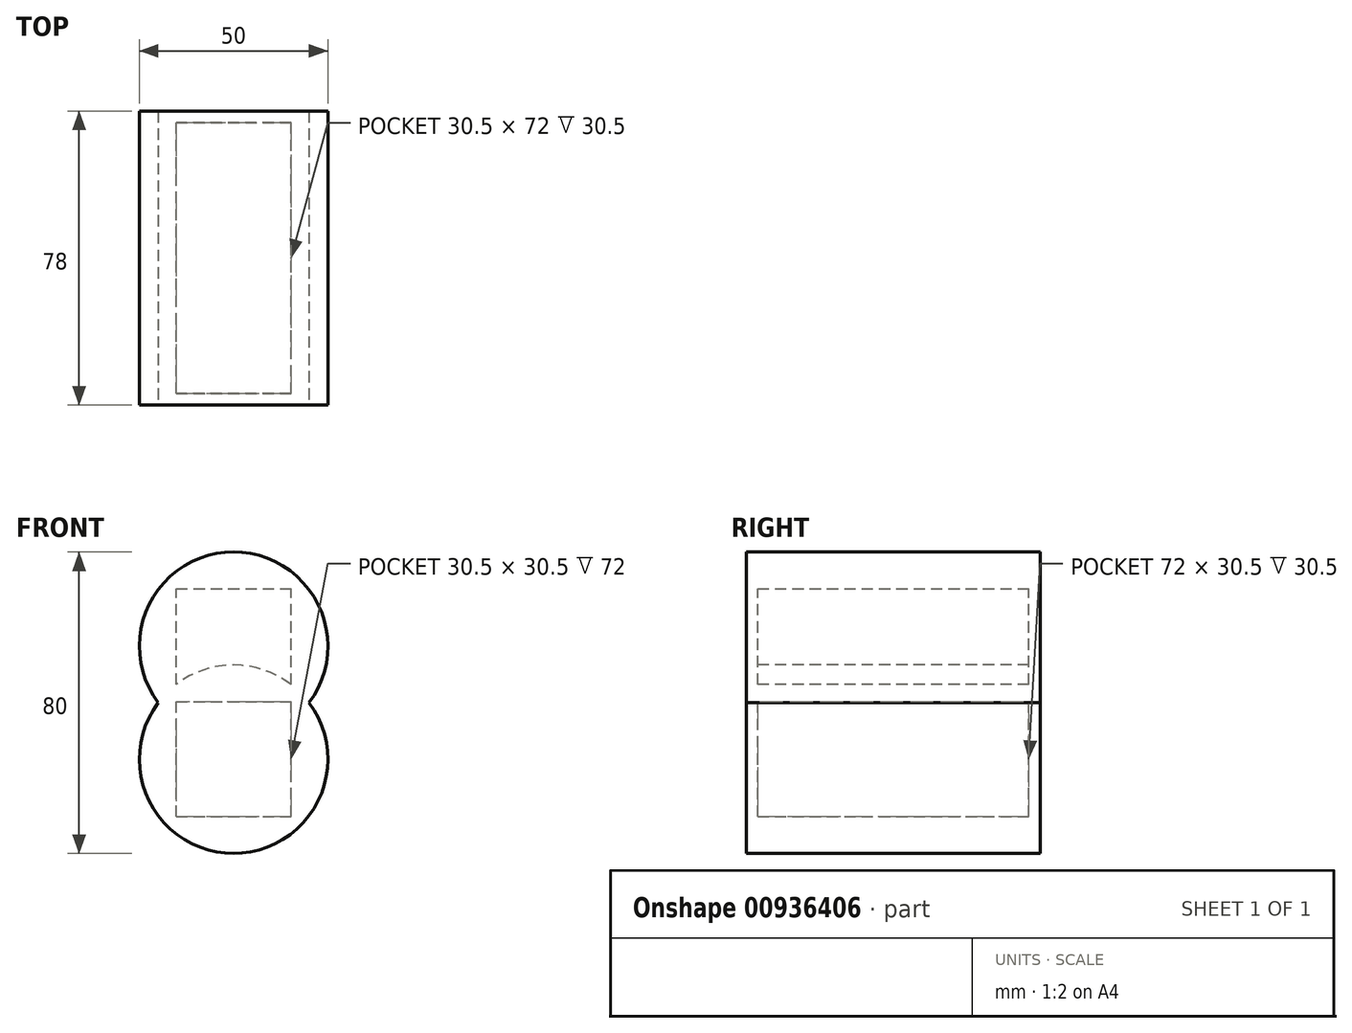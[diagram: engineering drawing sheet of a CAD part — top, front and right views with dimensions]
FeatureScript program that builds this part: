
annotation { "Feature Type Name" : "Feature", "Feature Type Description" : "" }
export const myFeature = defineFeature(function(context is Context, id is Id, definition is map)
    precondition{}
    {
        {
            var Q0;
            Q0=qCreatedBy(makeId("Front.planeOp"),FACE);
            var sketch = newSketch(context, id + "F0", { "sketchPlane" : qUnion([Q0])});
            skCircle(sketch, "E0", {"center": v(0, 0) * mm, "radius": 25 * mm});
            skSolve(sketch);
        }
        {
            var Q0;
            Q0 = qSketchRegion(id + "F0", true);
            extrude(context, id + "F1", {"entities" : qUnion([Q0]), "oppositeDirection" : true, "depth" : 75 * mm, "offsetDistance" : 25.4 * mm});
        }
        {
            var Q0;
            Q0=makeQuery(id+"F1.opExtrude","CAP_FACE",FACE,{"disambiguationData":[OSD([sQuery(id+"F0.wireOp",EDGE,"E0")])],"isStart":false});
            var sketch = newSketch(context, id + "F2", { "sketchPlane" : qUnion([Q0])});
            skLineSegment(sketch, "E1.bottom", {"start": v(15.25, -15.25) * mm, "end": v(-15.25, -15.25) * mm});
            skLineSegment(sketch, "E1.top", {"start": v(15.25, 15.25) * mm, "end": v(-15.25, 15.25) * mm});
            skLineSegment(sketch, "E1.left", {"start": v(15.25, -15.25) * mm, "end": v(15.25, 15.25) * mm});
            skLineSegment(sketch, "E1.right", {"start": v(-15.25, -15.25) * mm, "end": v(-15.25, 15.25) * mm});
            skPoint(sketch, "E1.middle", {"position": v(0, 0) * mm});
            skSolve(sketch);
        }
        {
            var Q0;
            Q0 = qSketchRegion(id + "F2", true);
            var Q1;
            Q1=makeQuery(id+"F1.opExtrude","CAP_FACE",FACE,{"disambiguationData":[OSD([sQuery(id+"F0.wireOp",EDGE,"E0")])],"isStart":true});
            extrude(context, id + "F3", {"entities" : qUnion([Q0]), "operationType" : NewBodyOperationType.REMOVE, "endBound" : BoundingType.UP_TO_SURFACE, "oppositeDirection" : true, "depth" : 194 * mm, "endBoundEntityFace" : qUnion([Q1]), "hasOffset" : true, "offsetDistance" : 3 * mm});
        }
        {
            var Q0;
            Q0=makeQuery(id+"F1.opExtrude","CAP_FACE",FACE,{"disambiguationData":[OSD([sQuery(id+"F0.wireOp",EDGE,"E0")])],"isStart":false});
            var sketch = newSketch(context, id + "F4", { "sketchPlane" : qUnion([Q0])});
            skCircle(sketch, "E2", {"center": v(0, 0) * mm, "radius": 25 * mm});
            skSolve(sketch);
        }
        {
            var Q0;
            Q0 = qSketchRegion(id + "F4", true);
            extrude(context, id + "F5", {"entities" : qUnion([Q0]), "operationType" : NewBodyOperationType.ADD, "depth" : 3 * mm, "offsetDistance" : 25 * mm});
        }
        {
            var Q0;
            Q0=qCreatedBy(makeId("Front.planeOp"),FACE);
            var sketch = newSketch(context, id + "F6", { "sketchPlane" : qUnion([Q0])});
            skCircle(sketch, "E3", {"center": v(0, -30) * mm, "radius": 25 * mm});
            skSolve(sketch);
        }
        {
            var Q0;
            Q0 = qSketchRegion(id + "F6", true);
            extrude(context, id + "F7", {"entities" : qUnion([Q0]), "operationType" : NewBodyOperationType.ADD, "oppositeDirection" : true, "depth" : 75 * mm, "offsetDistance" : 25 * mm});
        }
        {
            var Q0;
            Q0=makeQuery(id+"F7.opExtrude","CAP_FACE",FACE,{"disambiguationData":[OSD([sQuery(id+"F6.wireOp",EDGE,"E3")])],"isStart":false});
            var sketch = newSketch(context, id + "F8", { "sketchPlane" : qUnion([Q0])});
            skLineSegment(sketch, "E4.bottom", {"start": v(15.25, -45.25) * mm, "end": v(-15.25, -45.25) * mm});
            skLineSegment(sketch, "E4.top", {"start": v(15.25, -14.75) * mm, "end": v(-15.25, -14.75) * mm});
            skLineSegment(sketch, "E4.left", {"start": v(15.25, -45.25) * mm, "end": v(15.25, -14.75) * mm});
            skLineSegment(sketch, "E4.right", {"start": v(-15.25, -45.25) * mm, "end": v(-15.25, -14.75) * mm});
            skPoint(sketch, "E4.middle", {"position": v(0, -30) * mm});
            skSolve(sketch);
        }
        {
            var Q0;
            Q0 = qSketchRegion(id + "F8", true);
            var Q1;
            Q1=makeQuery(id+"F7.boolean.opBoolean","MERGE",FACE,{"derivedFrom":[makeQuery(id+"F1.opExtrude","CAP_FACE",FACE,{"disambiguationData":[OSD([sQuery(id+"F0.wireOp",EDGE,"E0")])],"isStart":true}),makeQuery(id+"F7.opExtrude","CAP_FACE",FACE,{"disambiguationData":[OSD([sQuery(id+"F6.wireOp",EDGE,"E3")])],"isStart":true})]});
            extrude(context, id + "F9", {"entities" : qUnion([Q0]), "operationType" : NewBodyOperationType.REMOVE, "endBound" : BoundingType.UP_TO_SURFACE, "oppositeDirection" : true, "depth" : 25 * mm, "endBoundEntityFace" : qUnion([Q1]), "hasOffset" : true, "offsetDistance" : 3 * mm});
        }
        {
            var Q0;
            Q0=makeQuery(id+"F7.opExtrude","CAP_FACE",FACE,{"disambiguationData":[OSD([sQuery(id+"F6.wireOp",EDGE,"E3")])],"isStart":false});
            var sketch = newSketch(context, id + "F10", { "sketchPlane" : qUnion([Q0])});
            skCircle(sketch, "E5", {"center": v(0, -30) * mm, "radius": 25 * mm});
            skSolve(sketch);
        }
        {
            var Q0;
            Q0 = qSketchRegion(id + "F10", true);
            extrude(context, id + "F11", {"entities" : qUnion([Q0]), "operationType" : NewBodyOperationType.ADD, "depth" : 3 * mm, "offsetDistance" : 25 * mm});
        }
    });
